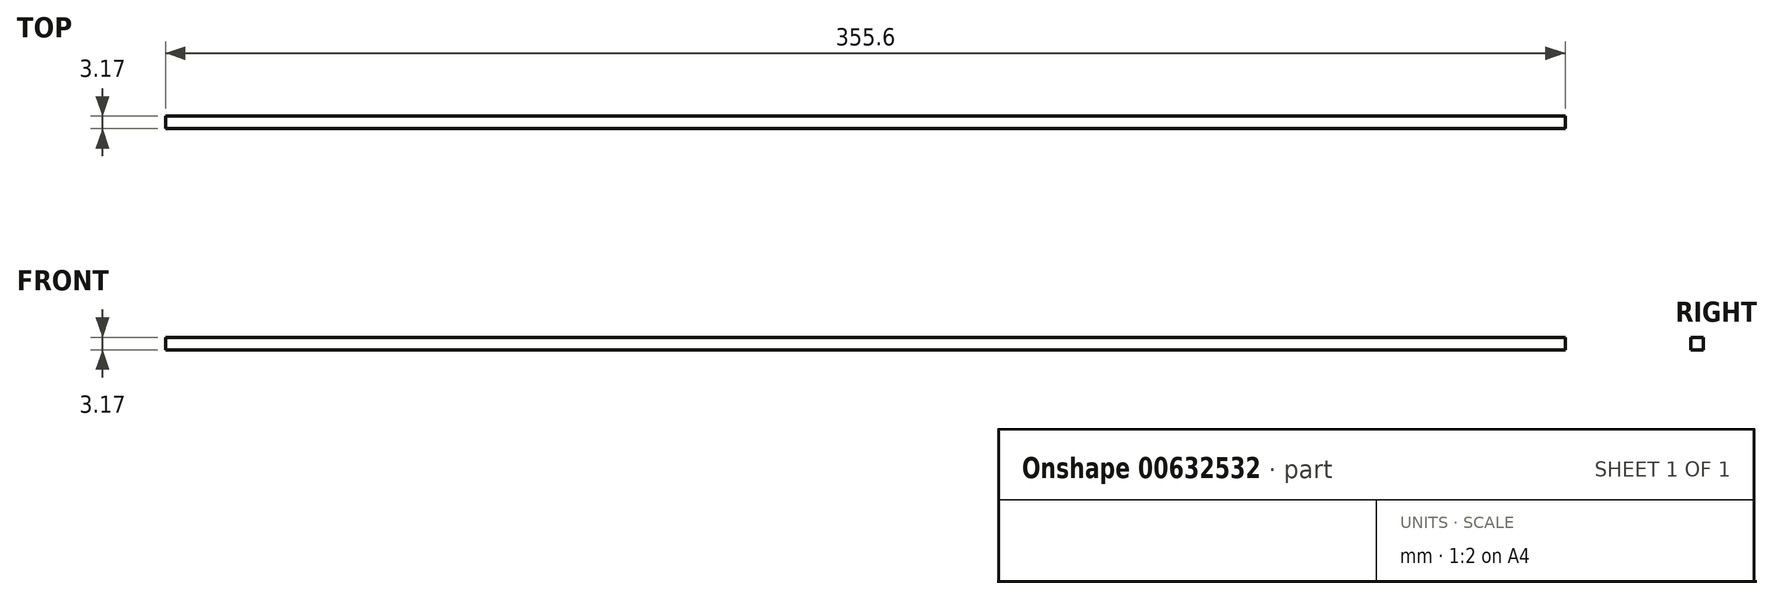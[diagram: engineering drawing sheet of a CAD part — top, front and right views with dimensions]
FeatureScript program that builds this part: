
annotation { "Feature Type Name" : "Feature", "Feature Type Description" : "" }
export const myFeature = defineFeature(function(context is Context, id is Id, definition is map)
    precondition{}
    {
        {
            var Q0;
            Q0=qCreatedBy(makeId("Top.planeOp"),FACE);
            var sketch = newSketch(context, id + "F0", { "sketchPlane" : qUnion([Q0])});
            skLineSegment(sketch, "E0", {"start": v(-183.14, 3.18) * mm, "end": v(172.46, 3.18) * mm});
            skLineSegment(sketch, "E1", {"start": v(172.46, 3.18) * mm, "end": v(172.46, 0) * mm});
            skLineSegment(sketch, "E2", {"start": v(172.46, 0) * mm, "end": v(-183.14, 0) * mm});
            skLineSegment(sketch, "E3", {"start": v(-183.14, 0) * mm, "end": v(-183.14, 3.18) * mm});
            skSolve(sketch);
        }
        {
            var Q0;
            Q0=makeQuery(id+"F0.imprint","IMPRINT",FACE,{"disambiguationData":[TD([[makeQuery(id+"F0.imprint","IMPRINT",EDGE,{"derivedFrom":sQuery(id+"F0.wireOp",EDGE,"E0")}),-1.0]])]});
            extrude(context, id + "F1", {"entities" : qUnion([Q0]), "depth" : 3.17 * mm, "offsetDistance" : 25.4 * mm});
        }
    });
